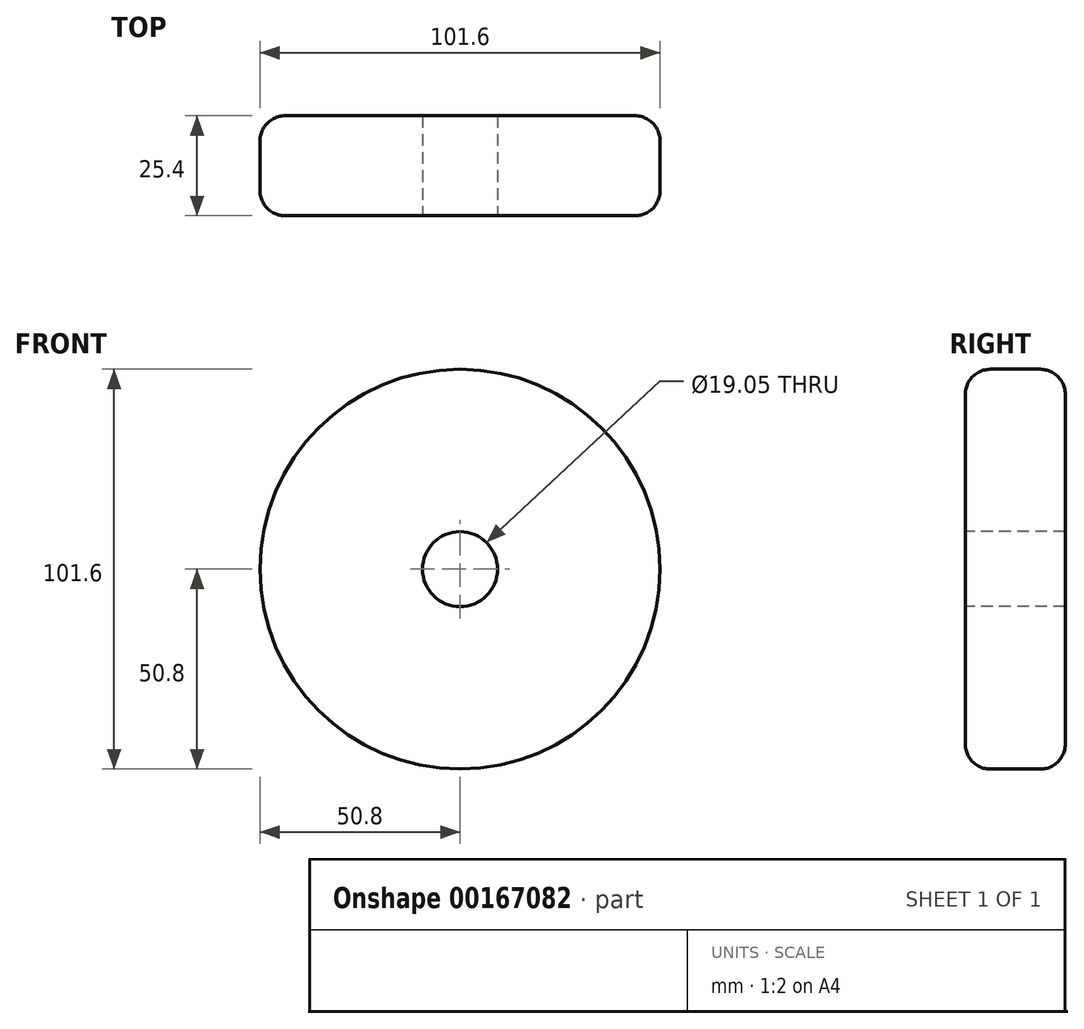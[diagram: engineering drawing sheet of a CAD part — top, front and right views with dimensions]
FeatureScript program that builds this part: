
annotation { "Feature Type Name" : "Feature", "Feature Type Description" : "" }
export const myFeature = defineFeature(function(context is Context, id is Id, definition is map)
    precondition{}
    {
        {
            var Q0;
            Q0=qCreatedBy(makeId("Front.planeOp"),FACE);
            var sketch = newSketch(context, id + "F0", { "sketchPlane" : qUnion([Q0])});
            skCircle(sketch, "E0", {"center": v(0, 0) * mm, "radius": 50.8 * mm});
            skSolve(sketch);
        }
        {
            var Q0;
            Q0 = qSketchRegion(id + "F0", true);
            extrude(context, id + "F1", {"entities" : qUnion([Q0]), "depth" : 25.4 * mm});
        }
        {
            var Q0;
            Q0=makeQuery(id+"F1.opExtrude","CAP_FACE",FACE,{"disambiguationData":[OSD([sQuery(id+"F0.wireOp",EDGE,"E0")])],"isStart":false});
            var sketch = newSketch(context, id + "F2", { "sketchPlane" : qUnion([Q0])});
            skCircle(sketch, "E1", {"center": v(0, 0) * mm, "radius": 9.53 * mm});
            skSolve(sketch);
        }
        {
            var Q0;
            Q0 = qSketchRegion(id + "F2", true);
            extrude(context, id + "F3", {"entities" : qUnion([Q0]), "operationType" : NewBodyOperationType.REMOVE, "endBound" : BoundingType.THROUGH_ALL, "oppositeDirection" : true, "depth" : 25.4 * mm});
        }
        {
            var Q0;
            Q0=makeQuery(id+"F1.opExtrude","CAP_EDGE",EDGE,{"disambiguationData":[OSD([sQuery(id+"F0.wireOp",EDGE,"E0")])],"isStart":false});
            var Q1;
            Q1=makeQuery(id+"F1.opExtrude","CAP_EDGE",EDGE,{"disambiguationData":[OSD([sQuery(id+"F0.wireOp",EDGE,"E0")])],"isStart":true});
            fillet(context, id + "F4", {"entities" : qUnion([Q0, Q1]), "radius" : 6.35 * mm, "tangentPropagation" : true, "allowEdgeOverflow" : false});
        }
    });
